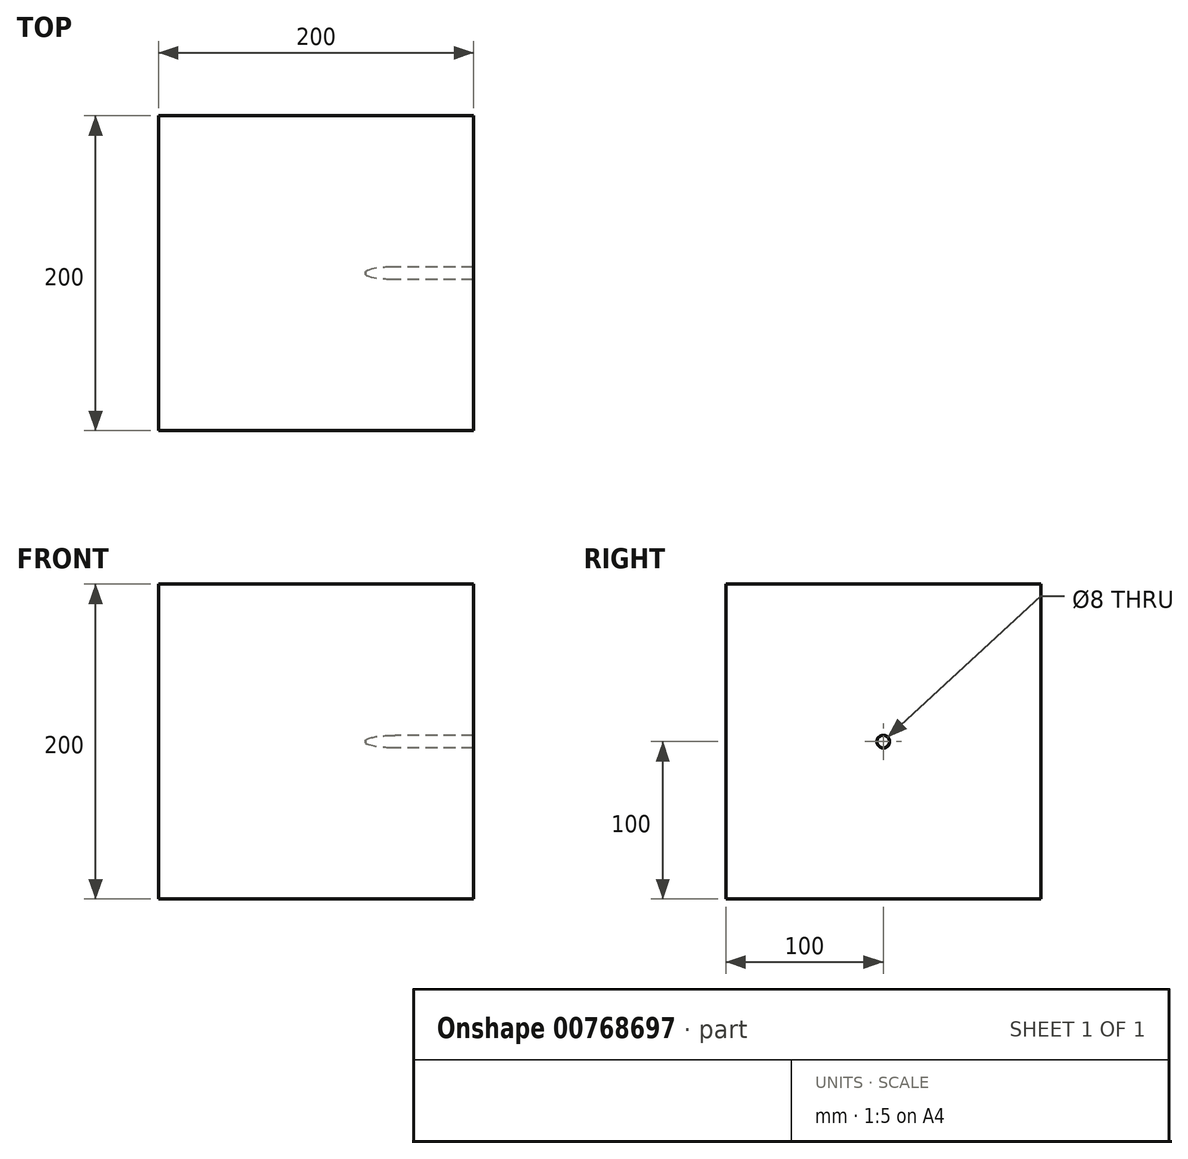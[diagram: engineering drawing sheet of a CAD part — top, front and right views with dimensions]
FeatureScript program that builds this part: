
annotation { "Feature Type Name" : "Feature", "Feature Type Description" : "" }
export const myFeature = defineFeature(function(context is Context, id is Id, definition is map)
    precondition{}
    {
        {
            var Q0;
            Q0=qCreatedBy(makeId("Front.planeOp"),FACE);
            var sketch = newSketch(context, id + "F0", { "sketchPlane" : qUnion([Q0])});
            skLineSegment(sketch, "E0", {"start": v(0, 0) * mm, "end": v(0, 1) * mm});
            skFitSpline(sketch, "E1", {"points": [v(0, 1) * mm, v(4.19, 2.72) * mm, v(11.66, 3.76) * mm, v(18.47, 4) * mm], "startDerivative": vector(0, 5.17) * mm, "endDerivative": vector(25.21, 0) * mm});
            skLineSegment(sketch, "E2", {"start": v(18.47, 4) * mm, "end": v(68.47, 4) * mm});
            skLineSegment(sketch, "E3", {"start": v(68.47, 4) * mm, "end": v(68.47, 0) * mm});
            skLineSegment(sketch, "E4", {"start": v(0, 0) * mm, "end": v(68.47, 0) * mm});
            skSolve(sketch);
        }
        {
            var Q0;
            Q0=makeQuery(id+"F0.imprint","IMPRINT",FACE,{"disambiguationData":[TD([[makeQuery(id+"F0.imprint","IMPRINT",EDGE,{"derivedFrom":sQuery(id+"F0.wireOp",EDGE,"E0")}),-1.0]])]});
            var Q1;
            Q1=sQuery(id+"F0.wireOp",EDGE,"E4");
            revolve(context, id + "F1", {"surfaceOperationType" : NewSurfaceOperationType.NEW, "entities" : qUnion([Q0]), "axis" : qUnion([Q1]), "revolveType" : RevolveType.FULL});
        }
        {
            var Q0;
            Q0=makeQuery(id+"F1.opRevolve","SWEPT_FACE",FACE,{"disambiguationData":[OSD([sQuery(id+"F0.wireOp",EDGE,"E3")])]});
            var sketch = newSketch(context, id + "F2", { "sketchPlane" : qUnion([Q0])});
            skLineSegment(sketch, "E5.bottom", {"start": v(-100, 100) * mm, "end": v(100, 100) * mm});
            skLineSegment(sketch, "E5.top", {"start": v(-100, -100) * mm, "end": v(100, -100) * mm});
            skLineSegment(sketch, "E5.left", {"start": v(-100, 100) * mm, "end": v(-100, -100) * mm});
            skLineSegment(sketch, "E5.right", {"start": v(100, 100) * mm, "end": v(100, -100) * mm});
            skPoint(sketch, "E5.middle", {"position": v(0, 0) * mm});
            skSolve(sketch);
        }
        {
            var Q0;
            Q0 = qSketchRegion(id + "F2", true);
            extrude(context, id + "F3", {"entities" : qUnion([Q0]), "oppositeDirection" : true, "depth" : 200 * mm, "offsetDistance" : 25 * mm});
        }
        {
            var Q0;
            Q0=makeQuery(id+"F1.opRevolve","SWEPT_BODY",BODY,{"disambiguationData":[OSD([sQuery(id+"F0.wireOp",EDGE,"E0"),sQuery(id+"F0.wireOp",EDGE,"E1"),sQuery(id+"F0.wireOp",EDGE,"E2"),sQuery(id+"F0.wireOp",EDGE,"E3"),sQuery(id+"F0.wireOp",EDGE,"E4")])]});
            var Q1;
            Q1=makeQuery(id+"F3.opExtrude","SWEPT_BODY",BODY,{"disambiguationData":[OSD([sQuery(id+"F2.wireOp",EDGE,"E5.bottom"),sQuery(id+"F2.wireOp",EDGE,"E5.top"),sQuery(id+"F2.wireOp",EDGE,"E5.left"),sQuery(id+"F2.wireOp",EDGE,"E5.right")])]});
            booleanBodies(context, id + "F4", {"operationType" : BooleanOperationType.SUBTRACTION, "tools" : qUnion([Q0]), "targets" : qUnion([Q1])});
        }
    });
